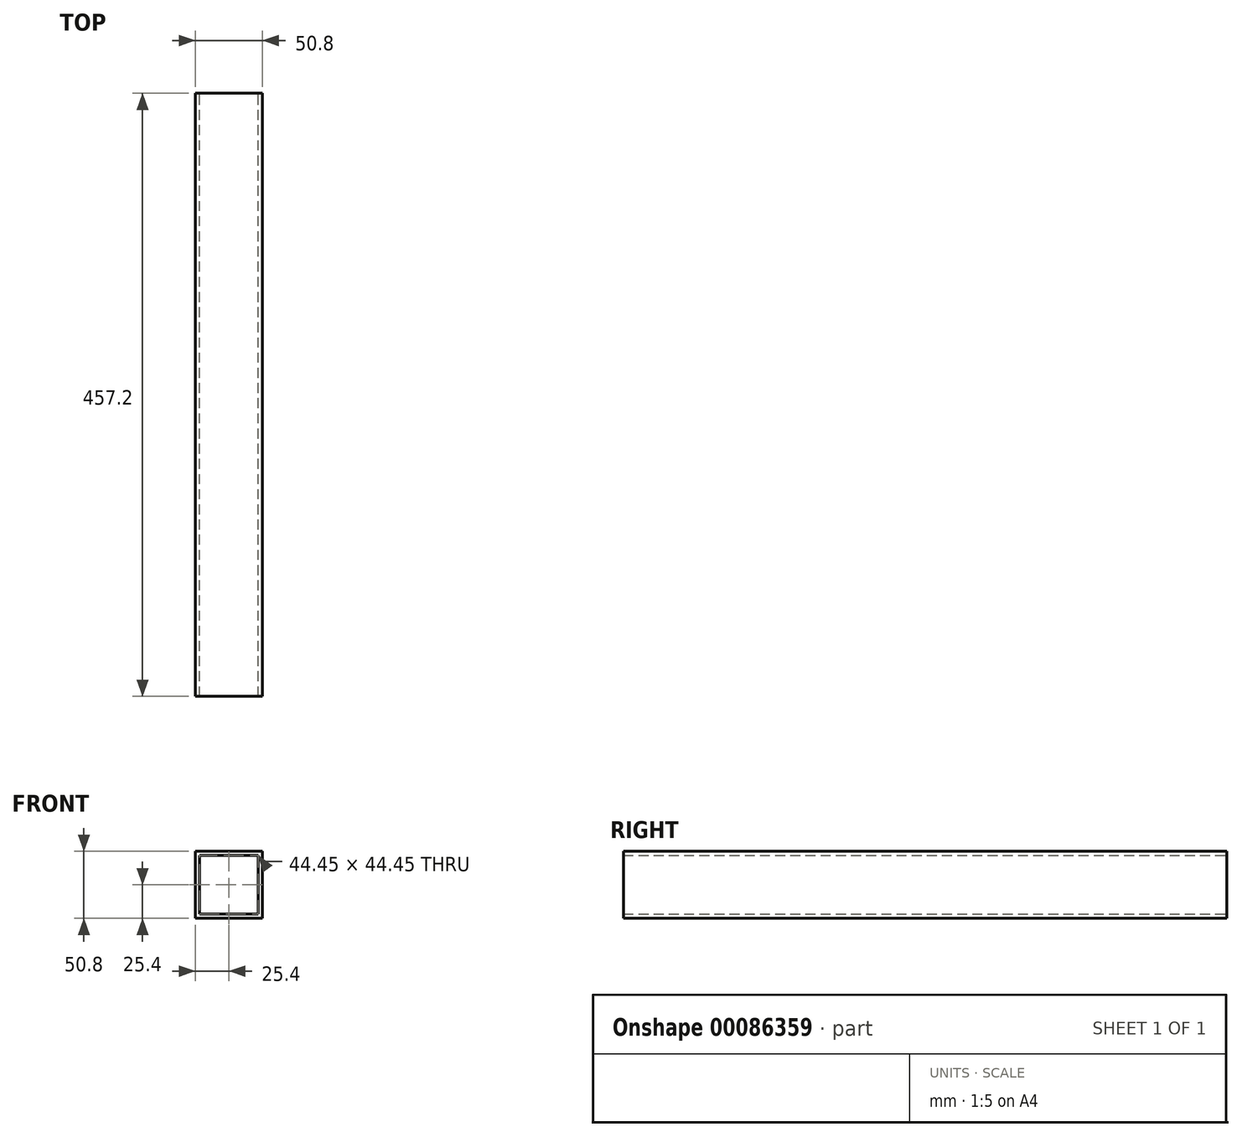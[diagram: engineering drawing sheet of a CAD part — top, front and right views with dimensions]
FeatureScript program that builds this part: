
annotation { "Feature Type Name" : "Feature", "Feature Type Description" : "" }
export const myFeature = defineFeature(function(context is Context, id is Id, definition is map)
    precondition{}
    {
        {
            var Q0;
            Q0=qCreatedBy(makeId("Front.planeOp"),FACE);
            var sketch = newSketch(context, id + "F0", { "sketchPlane" : qUnion([Q0])});
            skLineSegment(sketch, "E0.bottom", {"start": v(22.23, 22.22) * mm, "end": v(-22.23, 22.22) * mm});
            skLineSegment(sketch, "E0.top", {"start": v(22.23, -22.23) * mm, "end": v(-22.23, -22.23) * mm});
            skLineSegment(sketch, "E0.left", {"start": v(22.23, 22.22) * mm, "end": v(22.23, -22.23) * mm});
            skLineSegment(sketch, "E0.right", {"start": v(-22.23, 22.23) * mm, "end": v(-22.23, -22.23) * mm});
            skPoint(sketch, "E0.middle", {"position": v(0, 0) * mm});
            skLineSegment(sketch, "E1.0", {"start": v(25.4, 25.4) * mm, "end": v(-25.4, 25.4) * mm});
            skLineSegment(sketch, "E1.1", {"start": v(25.4, 25.4) * mm, "end": v(25.4, -25.4) * mm});
            skLineSegment(sketch, "E1.2", {"start": v(25.4, -25.4) * mm, "end": v(-25.4, -25.4) * mm});
            skLineSegment(sketch, "E1.3", {"start": v(-25.4, 25.4) * mm, "end": v(-25.4, -25.4) * mm});
            skSolve(sketch);
        }
        {
            var Q0;
            Q0 = qSketchRegion(id + "F0", true);
            extrude(context, id + "F1", {"entities" : qUnion([Q0]), "depth" : 457.2 * mm});
        }
    });
